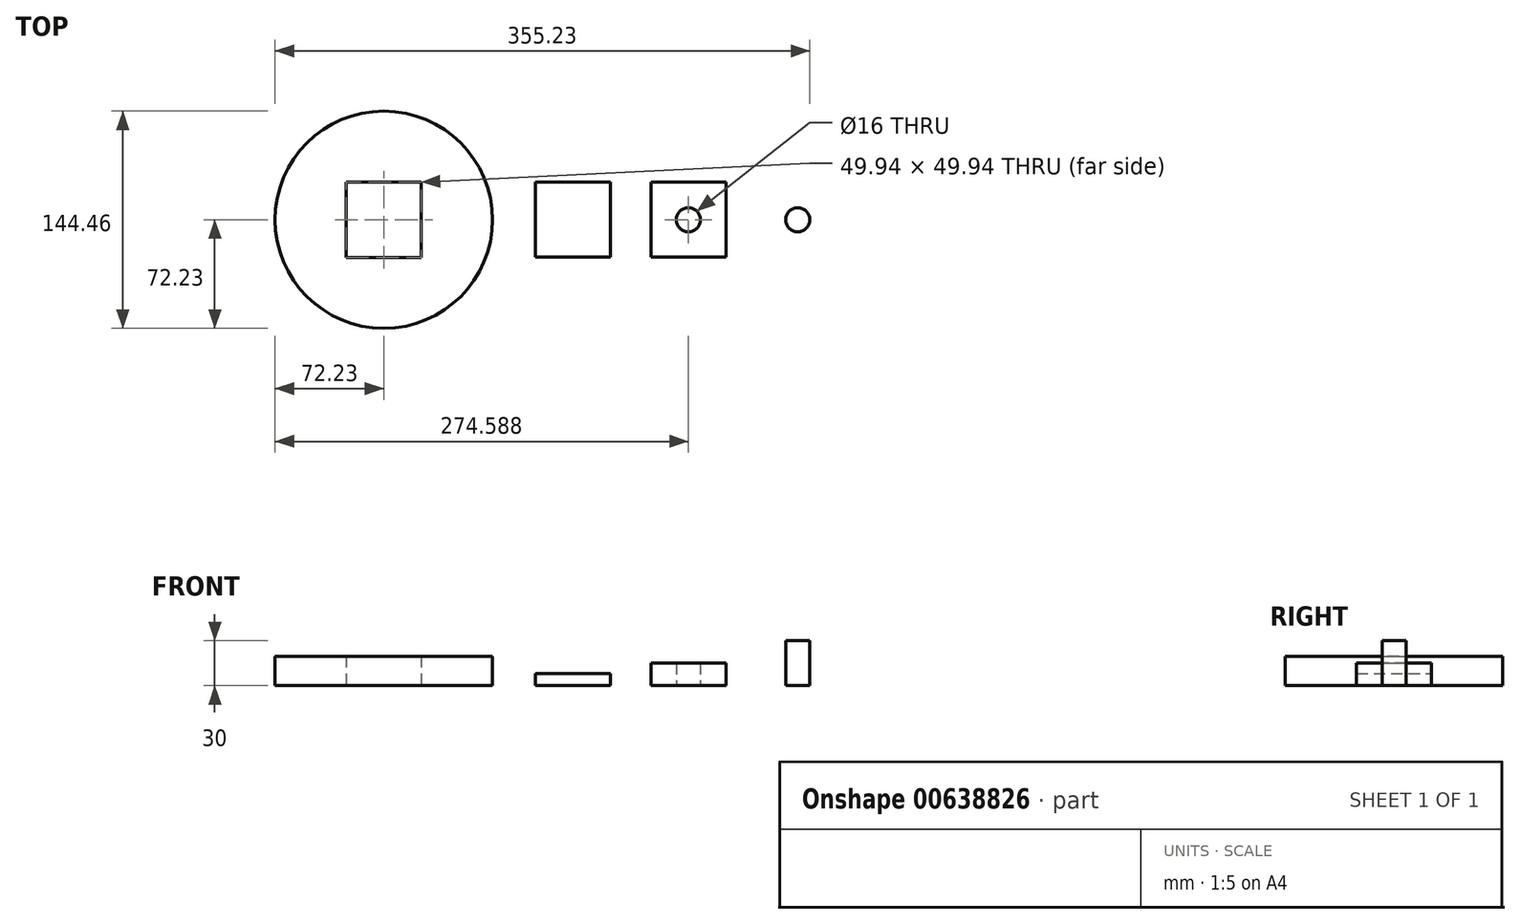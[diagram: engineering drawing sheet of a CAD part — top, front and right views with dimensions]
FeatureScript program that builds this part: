
annotation { "Feature Type Name" : "Feature", "Feature Type Description" : "" }
export const myFeature = defineFeature(function(context is Context, id is Id, definition is map)
    precondition{}
    {
        {
            var Q0;
            Q0=qCreatedBy(makeId("Top.planeOp"),FACE);
            var sketch = newSketch(context, id + "F0", { "sketchPlane" : qUnion([Q0])});
            skCircle(sketch, "E0", {"center": v(0, 0) * mm, "radius": 72.22 * mm});
            skLineSegment(sketch, "E1.bottom", {"start": v(24.97, -24.97) * mm, "end": v(-24.97, -24.97) * mm});
            skLineSegment(sketch, "E1.top", {"start": v(24.97, 24.97) * mm, "end": v(-24.97, 24.97) * mm});
            skLineSegment(sketch, "E1.left", {"start": v(24.97, -24.97) * mm, "end": v(24.97, 24.97) * mm});
            skLineSegment(sketch, "E1.right", {"start": v(-24.97, -24.97) * mm, "end": v(-24.97, 24.97) * mm});
            skSolve(sketch);
        }
        {
            var Q0;
            Q0 = qSketchRegion(id + "F0", true);
            var Q1;
            Q1=makeQuery(id+"F0.imprint","IMPRINT",FACE,{"disambiguationData":[TD([[makeQuery(id+"F0.imprint","IMPRINT",EDGE,{"derivedFrom":sQuery(id+"F0.wireOp",EDGE,"E0")}),1.0]])]});
            extrude(context, id + "F1", {"entities" : qUnion([Q0, Q1]), "depth" : 19.6 * mm, "offsetDistance" : 25 * mm});
        }
        {
            var Q0;
            Q0=qCreatedBy(makeId("Top.planeOp"),FACE);
            var sketch = newSketch(context, id + "F2", { "sketchPlane" : qUnion([Q0])});
            skLineSegment(sketch, "E2.bottom", {"start": v(150.68, -24.95) * mm, "end": v(100.78, -24.95) * mm});
            skLineSegment(sketch, "E2.top", {"start": v(150.68, 24.95) * mm, "end": v(100.78, 24.95) * mm});
            skLineSegment(sketch, "E2.left", {"start": v(150.68, -24.95) * mm, "end": v(150.68, 24.95) * mm});
            skLineSegment(sketch, "E2.right", {"start": v(100.78, -24.95) * mm, "end": v(100.78, 24.95) * mm});
            skPoint(sketch, "E2.middle", {"position": v(125.73, 0) * mm});
            skSolve(sketch);
        }
        {
            var Q0;
            Q0=makeQuery(id+"F2.imprint","IMPRINT",FACE,{"disambiguationData":[TD([[makeQuery(id+"F2.imprint","IMPRINT",EDGE,{"derivedFrom":sQuery(id+"F2.wireOp",EDGE,"E2.bottom")}),-1.0]])]});
            extrude(context, id + "F3", {"entities" : qUnion([Q0]), "depth" : 8 * mm, "offsetDistance" : 25 * mm});
        }
        {
            var Q0;
            Q0=qCreatedBy(makeId("Top.planeOp"),FACE);
            var sketch = newSketch(context, id + "F4", { "sketchPlane" : qUnion([Q0])});
            skLineSegment(sketch, "E3.bottom", {"start": v(177.4, -24.95) * mm, "end": v(227.3, -24.95) * mm});
            skLineSegment(sketch, "E3.top", {"start": v(177.4, 24.95) * mm, "end": v(227.3, 24.95) * mm});
            skLineSegment(sketch, "E3.left", {"start": v(177.4, -24.95) * mm, "end": v(177.4, 24.95) * mm});
            skLineSegment(sketch, "E3.right", {"start": v(227.3, -24.95) * mm, "end": v(227.3, 24.95) * mm});
            skPoint(sketch, "E3.middle", {"position": v(202.36, 0) * mm});
            skCircle(sketch, "E4", {"center": v(202.36, 0) * mm, "radius": 8 * mm});
            skSolve(sketch);
        }
        {
            var Q0;
            Q0 = qSketchRegion(id + "F4", true);
            extrude(context, id + "F5", {"entities" : qUnion([Q0]), "depth" : 15 * mm, "offsetDistance" : 25 * mm});
        }
        {
            var Q0;
            Q0=qCreatedBy(makeId("Top.planeOp"),FACE);
            var sketch = newSketch(context, id + "F6", { "sketchPlane" : qUnion([Q0])});
            skCircle(sketch, "E5", {"center": v(275, 0) * mm, "radius": 8 * mm});
            skSolve(sketch);
        }
        {
            var Q0;
            Q0 = qSketchRegion(id + "F6", true);
            extrude(context, id + "F7", {"entities" : qUnion([Q0]), "depth" : 30 * mm, "offsetDistance" : 25 * mm});
        }
    });
